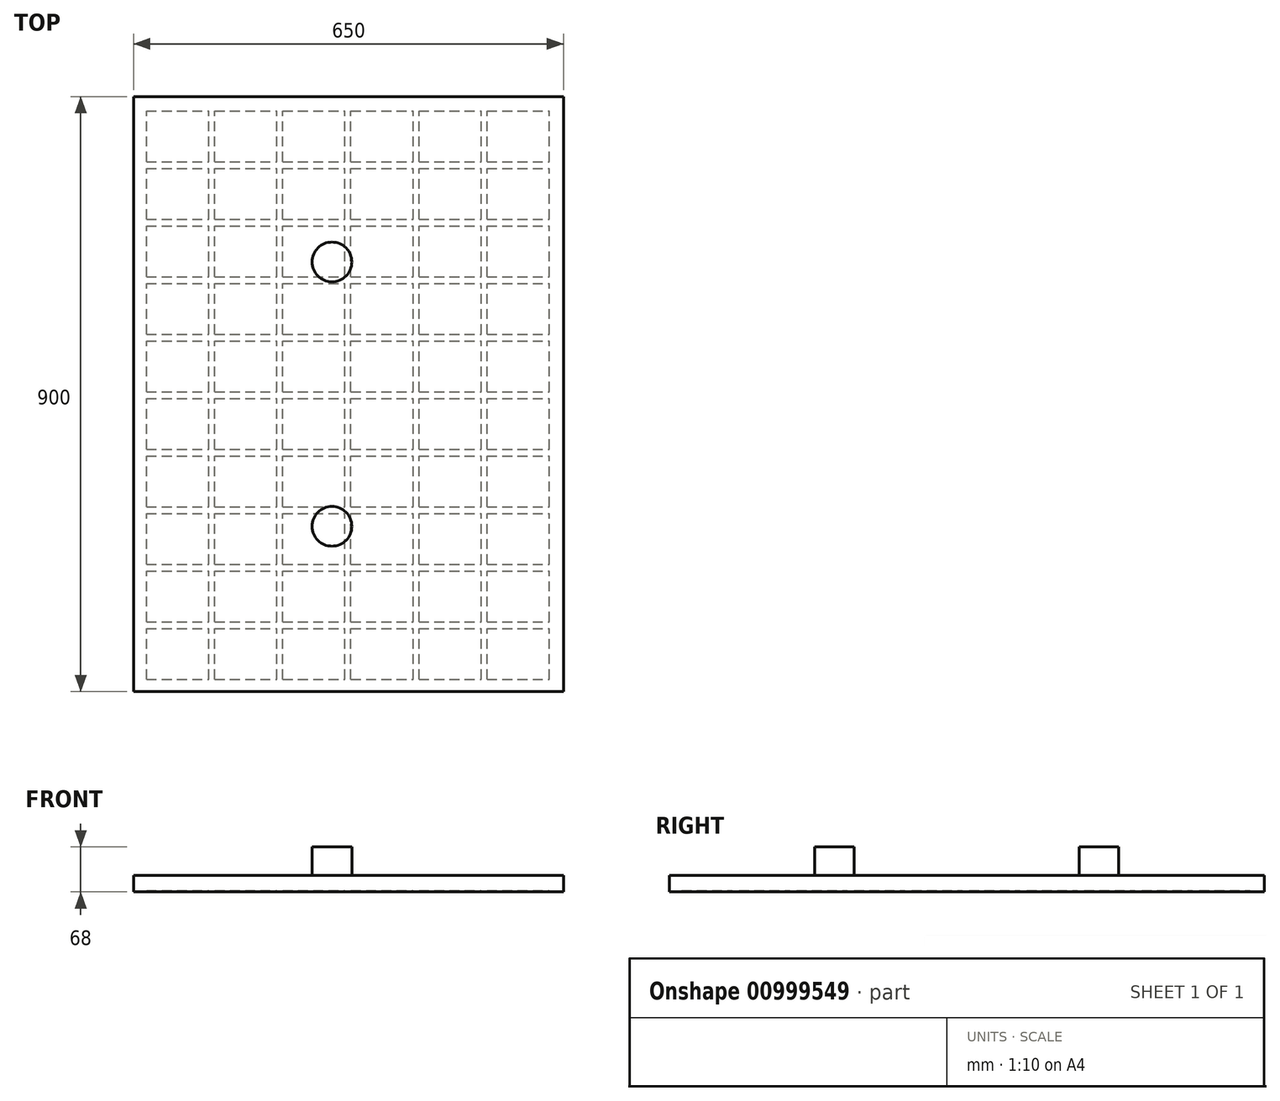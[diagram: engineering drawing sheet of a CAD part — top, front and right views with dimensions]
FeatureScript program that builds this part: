
annotation { "Feature Type Name" : "Feature", "Feature Type Description" : "" }
export const myFeature = defineFeature(function(context is Context, id is Id, definition is map)
    precondition{}
    {
        {
            var Q0;
            Q0=qCreatedBy(makeId("Top.planeOp"),FACE);
            var sketch = newSketch(context, id + "F0", { "sketchPlane" : qUnion([Q0])});
            skLineSegment(sketch, "E0.bottom", {"start": v(-300, 450) * mm, "end": v(350, 450) * mm});
            skLineSegment(sketch, "E0.top", {"start": v(-300, -450) * mm, "end": v(350, -450) * mm});
            skLineSegment(sketch, "E0.left", {"start": v(-300, 450) * mm, "end": v(-300, -450) * mm});
            skLineSegment(sketch, "E0.right", {"start": v(350, 450) * mm, "end": v(350, -450) * mm});
            skSolve(sketch);
        }
        {
            var Q0;
            Q0 = qSketchRegion(id + "F0", true);
            extrude(context, id + "F1", {"entities" : qUnion([Q0]), "depth" : 25 * mm, "offsetDistance" : 25 * mm});
        }
        {
            var Q0;
            Q0=makeQuery(id+"F1.opExtrude","CAP_FACE",FACE,{"disambiguationData":[OSD([sQuery(id+"F0.wireOp",EDGE,"E0.bottom"),sQuery(id+"F0.wireOp",EDGE,"E0.top"),sQuery(id+"F0.wireOp",EDGE,"E0.left"),sQuery(id+"F0.wireOp",EDGE,"E0.right")])],"isStart":false});
            var sketch = newSketch(context, id + "F2", { "sketchPlane" : qUnion([Q0])});
            skCircle(sketch, "E1", {"center": v(0, 200) * mm, "radius": 30 * mm});
            skCircle(sketch, "E2", {"center": v(0, -200) * mm, "radius": 30 * mm});
            skSolve(sketch);
        }
        {
            var Q0;
            Q0 = qSketchRegion(id + "F2", true);
            extrude(context, id + "F3", {"entities" : qUnion([Q0]), "operationType" : NewBodyOperationType.ADD, "depth" : 43 * mm, "offsetDistance" : 25 * mm});
        }
        {
            var Q0;
            Q0=makeQuery(id+"F1.opExtrude","CAP_FACE",FACE,{"disambiguationData":[OSD([sQuery(id+"F0.wireOp",EDGE,"E0.bottom"),sQuery(id+"F0.wireOp",EDGE,"E0.top"),sQuery(id+"F0.wireOp",EDGE,"E0.left"),sQuery(id+"F0.wireOp",EDGE,"E0.right")])],"isStart":true});
            var sketch = newSketch(context, id + "F4", { "sketchPlane" : qUnion([Q0])});
            skLineSegment(sketch, "E3.bottom", {"start": v(-280.37, 431.23) * mm, "end": v(-186.33, 431.23) * mm});
            skLineSegment(sketch, "E3.top", {"start": v(-280.37, 354.51) * mm, "end": v(-186.33, 354.51) * mm});
            skLineSegment(sketch, "E3.left", {"start": v(-280.37, 431.23) * mm, "end": v(-280.37, 354.51) * mm});
            skLineSegment(sketch, "E3.right", {"start": v(-186.33, 431.23) * mm, "end": v(-186.33, 354.51) * mm});
            skLineSegment(sketch, "E4.0.1.0", {"start": v(-280.37, 344.23) * mm, "end": v(-186.33, 344.23) * mm});
            skLineSegment(sketch, "E4.0.1.1", {"start": v(-186.33, 344.23) * mm, "end": v(-186.33, 267.51) * mm});
            skLineSegment(sketch, "E4.0.1.2", {"start": v(-280.37, 267.51) * mm, "end": v(-186.33, 267.51) * mm});
            skLineSegment(sketch, "E4.0.1.3", {"start": v(-280.37, 344.23) * mm, "end": v(-280.37, 267.51) * mm});
            skLineSegment(sketch, "E4.0.2.0", {"start": v(-280.37, 257.23) * mm, "end": v(-186.33, 257.23) * mm});
            skLineSegment(sketch, "E4.0.2.1", {"start": v(-186.33, 257.23) * mm, "end": v(-186.33, 180.51) * mm});
            skLineSegment(sketch, "E4.0.2.2", {"start": v(-280.37, 180.51) * mm, "end": v(-186.33, 180.51) * mm});
            skLineSegment(sketch, "E4.0.2.3", {"start": v(-280.37, 257.23) * mm, "end": v(-280.37, 180.51) * mm});
            skLineSegment(sketch, "E4.0.3.0", {"start": v(-280.37, 170.23) * mm, "end": v(-186.33, 170.23) * mm});
            skLineSegment(sketch, "E4.0.3.1", {"start": v(-186.33, 170.23) * mm, "end": v(-186.33, 93.51) * mm});
            skLineSegment(sketch, "E4.0.3.2", {"start": v(-280.37, 93.51) * mm, "end": v(-186.33, 93.51) * mm});
            skLineSegment(sketch, "E4.0.3.3", {"start": v(-280.37, 170.23) * mm, "end": v(-280.37, 93.51) * mm});
            skLineSegment(sketch, "E4.0.4.0", {"start": v(-280.37, 83.23) * mm, "end": v(-186.33, 83.23) * mm});
            skLineSegment(sketch, "E4.0.4.1", {"start": v(-186.33, 83.23) * mm, "end": v(-186.33, 6.51) * mm});
            skLineSegment(sketch, "E4.0.4.2", {"start": v(-280.37, 6.51) * mm, "end": v(-186.33, 6.51) * mm});
            skLineSegment(sketch, "E4.0.4.3", {"start": v(-280.37, 83.23) * mm, "end": v(-280.37, 6.51) * mm});
            skLineSegment(sketch, "E4.0.5.0", {"start": v(-280.37, -3.77) * mm, "end": v(-186.33, -3.77) * mm});
            skLineSegment(sketch, "E4.0.5.1", {"start": v(-186.33, -3.77) * mm, "end": v(-186.33, -80.49) * mm});
            skLineSegment(sketch, "E4.0.5.2", {"start": v(-280.37, -80.49) * mm, "end": v(-186.33, -80.49) * mm});
            skLineSegment(sketch, "E4.0.5.3", {"start": v(-280.37, -3.77) * mm, "end": v(-280.37, -80.49) * mm});
            skLineSegment(sketch, "E4.0.6.0", {"start": v(-280.37, -90.77) * mm, "end": v(-186.33, -90.77) * mm});
            skLineSegment(sketch, "E4.0.6.1", {"start": v(-186.33, -90.77) * mm, "end": v(-186.33, -167.49) * mm});
            skLineSegment(sketch, "E4.0.6.2", {"start": v(-280.37, -167.49) * mm, "end": v(-186.33, -167.49) * mm});
            skLineSegment(sketch, "E4.0.6.3", {"start": v(-280.37, -90.77) * mm, "end": v(-280.37, -167.49) * mm});
            skLineSegment(sketch, "E4.0.7.0", {"start": v(-280.37, -177.77) * mm, "end": v(-186.33, -177.77) * mm});
            skLineSegment(sketch, "E4.0.7.1", {"start": v(-186.33, -177.77) * mm, "end": v(-186.33, -254.49) * mm});
            skLineSegment(sketch, "E4.0.7.2", {"start": v(-280.37, -254.49) * mm, "end": v(-186.33, -254.49) * mm});
            skLineSegment(sketch, "E4.0.7.3", {"start": v(-280.37, -177.77) * mm, "end": v(-280.37, -254.49) * mm});
            skLineSegment(sketch, "E4.0.8.0", {"start": v(-280.37, -264.77) * mm, "end": v(-186.33, -264.77) * mm});
            skLineSegment(sketch, "E4.0.8.1", {"start": v(-186.33, -264.77) * mm, "end": v(-186.33, -341.49) * mm});
            skLineSegment(sketch, "E4.0.8.2", {"start": v(-280.37, -341.49) * mm, "end": v(-186.33, -341.49) * mm});
            skLineSegment(sketch, "E4.0.8.3", {"start": v(-280.37, -264.77) * mm, "end": v(-280.37, -341.49) * mm});
            skLineSegment(sketch, "E4.0.9.0", {"start": v(-280.37, -351.77) * mm, "end": v(-186.33, -351.77) * mm});
            skLineSegment(sketch, "E4.0.9.1", {"start": v(-186.33, -351.77) * mm, "end": v(-186.33, -428.49) * mm});
            skLineSegment(sketch, "E4.0.9.2", {"start": v(-280.37, -428.49) * mm, "end": v(-186.33, -428.49) * mm});
            skLineSegment(sketch, "E4.0.9.3", {"start": v(-280.37, -351.77) * mm, "end": v(-280.37, -428.49) * mm});
            skLineSegment(sketch, "E4.1.0.0", {"start": v(-177.37, 431.23) * mm, "end": v(-83.33, 431.23) * mm});
            skLineSegment(sketch, "E4.1.0.1", {"start": v(-83.33, 431.23) * mm, "end": v(-83.33, 354.51) * mm});
            skLineSegment(sketch, "E4.1.0.2", {"start": v(-177.37, 354.51) * mm, "end": v(-83.33, 354.51) * mm});
            skLineSegment(sketch, "E4.1.0.3", {"start": v(-177.37, 431.23) * mm, "end": v(-177.37, 354.51) * mm});
            skLineSegment(sketch, "E4.1.1.0", {"start": v(-177.37, 344.23) * mm, "end": v(-83.33, 344.23) * mm});
            skLineSegment(sketch, "E4.1.1.1", {"start": v(-83.33, 344.23) * mm, "end": v(-83.33, 267.51) * mm});
            skLineSegment(sketch, "E4.1.1.2", {"start": v(-177.37, 267.51) * mm, "end": v(-83.33, 267.51) * mm});
            skLineSegment(sketch, "E4.1.1.3", {"start": v(-177.37, 344.23) * mm, "end": v(-177.37, 267.51) * mm});
            skLineSegment(sketch, "E4.1.2.0", {"start": v(-177.37, 257.23) * mm, "end": v(-83.33, 257.23) * mm});
            skLineSegment(sketch, "E4.1.2.1", {"start": v(-83.33, 257.23) * mm, "end": v(-83.33, 180.51) * mm});
            skLineSegment(sketch, "E4.1.2.2", {"start": v(-177.37, 180.51) * mm, "end": v(-83.33, 180.51) * mm});
            skLineSegment(sketch, "E4.1.2.3", {"start": v(-177.37, 257.23) * mm, "end": v(-177.37, 180.51) * mm});
            skLineSegment(sketch, "E4.1.3.0", {"start": v(-177.37, 170.23) * mm, "end": v(-83.33, 170.23) * mm});
            skLineSegment(sketch, "E4.1.3.1", {"start": v(-83.33, 170.23) * mm, "end": v(-83.33, 93.51) * mm});
            skLineSegment(sketch, "E4.1.3.2", {"start": v(-177.37, 93.51) * mm, "end": v(-83.33, 93.51) * mm});
            skLineSegment(sketch, "E4.1.3.3", {"start": v(-177.37, 170.23) * mm, "end": v(-177.37, 93.51) * mm});
            skLineSegment(sketch, "E4.1.4.0", {"start": v(-177.37, 83.23) * mm, "end": v(-83.33, 83.23) * mm});
            skLineSegment(sketch, "E4.1.4.1", {"start": v(-83.33, 83.23) * mm, "end": v(-83.33, 6.51) * mm});
            skLineSegment(sketch, "E4.1.4.2", {"start": v(-177.37, 6.51) * mm, "end": v(-83.33, 6.51) * mm});
            skLineSegment(sketch, "E4.1.4.3", {"start": v(-177.37, 83.23) * mm, "end": v(-177.37, 6.51) * mm});
            skLineSegment(sketch, "E4.1.5.0", {"start": v(-177.37, -3.77) * mm, "end": v(-83.33, -3.77) * mm});
            skLineSegment(sketch, "E4.1.5.1", {"start": v(-83.33, -3.77) * mm, "end": v(-83.33, -80.49) * mm});
            skLineSegment(sketch, "E4.1.5.2", {"start": v(-177.37, -80.49) * mm, "end": v(-83.33, -80.49) * mm});
            skLineSegment(sketch, "E4.1.5.3", {"start": v(-177.37, -3.77) * mm, "end": v(-177.37, -80.49) * mm});
            skLineSegment(sketch, "E4.1.6.0", {"start": v(-177.37, -90.77) * mm, "end": v(-83.33, -90.77) * mm});
            skLineSegment(sketch, "E4.1.6.1", {"start": v(-83.33, -90.77) * mm, "end": v(-83.33, -167.49) * mm});
            skLineSegment(sketch, "E4.1.6.2", {"start": v(-177.37, -167.49) * mm, "end": v(-83.33, -167.49) * mm});
            skLineSegment(sketch, "E4.1.6.3", {"start": v(-177.37, -90.77) * mm, "end": v(-177.37, -167.49) * mm});
            skLineSegment(sketch, "E4.1.7.0", {"start": v(-177.37, -177.77) * mm, "end": v(-83.33, -177.77) * mm});
            skLineSegment(sketch, "E4.1.7.1", {"start": v(-83.33, -177.77) * mm, "end": v(-83.33, -254.49) * mm});
            skLineSegment(sketch, "E4.1.7.2", {"start": v(-177.37, -254.49) * mm, "end": v(-83.33, -254.49) * mm});
            skLineSegment(sketch, "E4.1.7.3", {"start": v(-177.37, -177.77) * mm, "end": v(-177.37, -254.49) * mm});
            skLineSegment(sketch, "E4.1.8.0", {"start": v(-177.37, -264.77) * mm, "end": v(-83.33, -264.77) * mm});
            skLineSegment(sketch, "E4.1.8.1", {"start": v(-83.33, -264.77) * mm, "end": v(-83.33, -341.49) * mm});
            skLineSegment(sketch, "E4.1.8.2", {"start": v(-177.37, -341.49) * mm, "end": v(-83.33, -341.49) * mm});
            skLineSegment(sketch, "E4.1.8.3", {"start": v(-177.37, -264.77) * mm, "end": v(-177.37, -341.49) * mm});
            skLineSegment(sketch, "E4.1.9.0", {"start": v(-177.37, -351.77) * mm, "end": v(-83.33, -351.77) * mm});
            skLineSegment(sketch, "E4.1.9.1", {"start": v(-83.33, -351.77) * mm, "end": v(-83.33, -428.49) * mm});
            skLineSegment(sketch, "E4.1.9.2", {"start": v(-177.37, -428.49) * mm, "end": v(-83.33, -428.49) * mm});
            skLineSegment(sketch, "E4.1.9.3", {"start": v(-177.37, -351.77) * mm, "end": v(-177.37, -428.49) * mm});
            skLineSegment(sketch, "E4.2.0.0", {"start": v(-74.37, 431.23) * mm, "end": v(19.67, 431.23) * mm});
            skLineSegment(sketch, "E4.2.0.1", {"start": v(19.67, 431.23) * mm, "end": v(19.67, 354.51) * mm});
            skLineSegment(sketch, "E4.2.0.2", {"start": v(-74.37, 354.51) * mm, "end": v(19.67, 354.51) * mm});
            skLineSegment(sketch, "E4.2.0.3", {"start": v(-74.37, 431.23) * mm, "end": v(-74.37, 354.51) * mm});
            skLineSegment(sketch, "E4.2.1.0", {"start": v(-74.37, 344.23) * mm, "end": v(19.67, 344.23) * mm});
            skLineSegment(sketch, "E4.2.1.1", {"start": v(19.67, 344.23) * mm, "end": v(19.67, 267.51) * mm});
            skLineSegment(sketch, "E4.2.1.2", {"start": v(-74.37, 267.51) * mm, "end": v(19.67, 267.51) * mm});
            skLineSegment(sketch, "E4.2.1.3", {"start": v(-74.37, 344.23) * mm, "end": v(-74.37, 267.51) * mm});
            skLineSegment(sketch, "E4.2.2.0", {"start": v(-74.37, 257.23) * mm, "end": v(19.67, 257.23) * mm});
            skLineSegment(sketch, "E4.2.2.1", {"start": v(19.67, 257.23) * mm, "end": v(19.67, 180.51) * mm});
            skLineSegment(sketch, "E4.2.2.2", {"start": v(-74.37, 180.51) * mm, "end": v(19.67, 180.51) * mm});
            skLineSegment(sketch, "E4.2.2.3", {"start": v(-74.37, 257.23) * mm, "end": v(-74.37, 180.51) * mm});
            skLineSegment(sketch, "E4.2.3.0", {"start": v(-74.37, 170.23) * mm, "end": v(19.67, 170.23) * mm});
            skLineSegment(sketch, "E4.2.3.1", {"start": v(19.67, 170.23) * mm, "end": v(19.67, 93.51) * mm});
            skLineSegment(sketch, "E4.2.3.2", {"start": v(-74.37, 93.51) * mm, "end": v(19.67, 93.51) * mm});
            skLineSegment(sketch, "E4.2.3.3", {"start": v(-74.37, 170.23) * mm, "end": v(-74.37, 93.51) * mm});
            skLineSegment(sketch, "E4.2.4.0", {"start": v(-74.37, 83.23) * mm, "end": v(19.67, 83.23) * mm});
            skLineSegment(sketch, "E4.2.4.1", {"start": v(19.67, 83.23) * mm, "end": v(19.67, 6.51) * mm});
            skLineSegment(sketch, "E4.2.4.2", {"start": v(-74.37, 6.51) * mm, "end": v(19.67, 6.51) * mm});
            skLineSegment(sketch, "E4.2.4.3", {"start": v(-74.37, 83.23) * mm, "end": v(-74.37, 6.51) * mm});
            skLineSegment(sketch, "E4.2.5.0", {"start": v(-74.37, -3.77) * mm, "end": v(19.67, -3.77) * mm});
            skLineSegment(sketch, "E4.2.5.1", {"start": v(19.67, -3.77) * mm, "end": v(19.67, -80.49) * mm});
            skLineSegment(sketch, "E4.2.5.2", {"start": v(-74.37, -80.49) * mm, "end": v(19.67, -80.49) * mm});
            skLineSegment(sketch, "E4.2.5.3", {"start": v(-74.37, -3.77) * mm, "end": v(-74.37, -80.49) * mm});
            skLineSegment(sketch, "E4.2.6.0", {"start": v(-74.37, -90.77) * mm, "end": v(19.67, -90.77) * mm});
            skLineSegment(sketch, "E4.2.6.1", {"start": v(19.67, -90.77) * mm, "end": v(19.67, -167.49) * mm});
            skLineSegment(sketch, "E4.2.6.2", {"start": v(-74.37, -167.49) * mm, "end": v(19.67, -167.49) * mm});
            skLineSegment(sketch, "E4.2.6.3", {"start": v(-74.37, -90.77) * mm, "end": v(-74.37, -167.49) * mm});
            skLineSegment(sketch, "E4.2.7.0", {"start": v(-74.37, -177.77) * mm, "end": v(19.67, -177.77) * mm});
            skLineSegment(sketch, "E4.2.7.1", {"start": v(19.67, -177.77) * mm, "end": v(19.67, -254.49) * mm});
            skLineSegment(sketch, "E4.2.7.2", {"start": v(-74.37, -254.49) * mm, "end": v(19.67, -254.49) * mm});
            skLineSegment(sketch, "E4.2.7.3", {"start": v(-74.37, -177.77) * mm, "end": v(-74.37, -254.49) * mm});
            skLineSegment(sketch, "E4.2.8.0", {"start": v(-74.37, -264.77) * mm, "end": v(19.67, -264.77) * mm});
            skLineSegment(sketch, "E4.2.8.1", {"start": v(19.67, -264.77) * mm, "end": v(19.67, -341.49) * mm});
            skLineSegment(sketch, "E4.2.8.2", {"start": v(-74.37, -341.49) * mm, "end": v(19.67, -341.49) * mm});
            skLineSegment(sketch, "E4.2.8.3", {"start": v(-74.37, -264.77) * mm, "end": v(-74.37, -341.49) * mm});
            skLineSegment(sketch, "E4.2.9.0", {"start": v(-74.37, -351.77) * mm, "end": v(19.67, -351.77) * mm});
            skLineSegment(sketch, "E4.2.9.1", {"start": v(19.67, -351.77) * mm, "end": v(19.67, -428.49) * mm});
            skLineSegment(sketch, "E4.2.9.2", {"start": v(-74.37, -428.49) * mm, "end": v(19.67, -428.49) * mm});
            skLineSegment(sketch, "E4.2.9.3", {"start": v(-74.37, -351.77) * mm, "end": v(-74.37, -428.49) * mm});
            skLineSegment(sketch, "E4.3.0.0", {"start": v(28.63, 431.23) * mm, "end": v(122.67, 431.23) * mm});
            skLineSegment(sketch, "E4.3.0.1", {"start": v(122.67, 431.23) * mm, "end": v(122.67, 354.51) * mm});
            skLineSegment(sketch, "E4.3.0.2", {"start": v(28.63, 354.51) * mm, "end": v(122.67, 354.51) * mm});
            skLineSegment(sketch, "E4.3.0.3", {"start": v(28.63, 431.23) * mm, "end": v(28.63, 354.51) * mm});
            skLineSegment(sketch, "E4.3.1.0", {"start": v(28.63, 344.23) * mm, "end": v(122.67, 344.23) * mm});
            skLineSegment(sketch, "E4.3.1.1", {"start": v(122.67, 344.23) * mm, "end": v(122.67, 267.51) * mm});
            skLineSegment(sketch, "E4.3.1.2", {"start": v(28.63, 267.51) * mm, "end": v(122.67, 267.51) * mm});
            skLineSegment(sketch, "E4.3.1.3", {"start": v(28.63, 344.23) * mm, "end": v(28.63, 267.51) * mm});
            skLineSegment(sketch, "E4.3.2.0", {"start": v(28.63, 257.23) * mm, "end": v(122.67, 257.23) * mm});
            skLineSegment(sketch, "E4.3.2.1", {"start": v(122.67, 257.23) * mm, "end": v(122.67, 180.51) * mm});
            skLineSegment(sketch, "E4.3.2.2", {"start": v(28.63, 180.51) * mm, "end": v(122.67, 180.51) * mm});
            skLineSegment(sketch, "E4.3.2.3", {"start": v(28.63, 257.23) * mm, "end": v(28.63, 180.51) * mm});
            skLineSegment(sketch, "E4.3.3.0", {"start": v(28.63, 170.23) * mm, "end": v(122.67, 170.23) * mm});
            skLineSegment(sketch, "E4.3.3.1", {"start": v(122.67, 170.23) * mm, "end": v(122.67, 93.51) * mm});
            skLineSegment(sketch, "E4.3.3.2", {"start": v(28.63, 93.51) * mm, "end": v(122.67, 93.51) * mm});
            skLineSegment(sketch, "E4.3.3.3", {"start": v(28.63, 170.23) * mm, "end": v(28.63, 93.51) * mm});
            skLineSegment(sketch, "E4.3.4.0", {"start": v(28.63, 83.23) * mm, "end": v(122.67, 83.23) * mm});
            skLineSegment(sketch, "E4.3.4.1", {"start": v(122.67, 83.23) * mm, "end": v(122.67, 6.51) * mm});
            skLineSegment(sketch, "E4.3.4.2", {"start": v(28.63, 6.51) * mm, "end": v(122.67, 6.51) * mm});
            skLineSegment(sketch, "E4.3.4.3", {"start": v(28.63, 83.23) * mm, "end": v(28.63, 6.51) * mm});
            skLineSegment(sketch, "E4.3.5.0", {"start": v(28.63, -3.77) * mm, "end": v(122.67, -3.77) * mm});
            skLineSegment(sketch, "E4.3.5.1", {"start": v(122.67, -3.77) * mm, "end": v(122.67, -80.49) * mm});
            skLineSegment(sketch, "E4.3.5.2", {"start": v(28.63, -80.49) * mm, "end": v(122.67, -80.49) * mm});
            skLineSegment(sketch, "E4.3.5.3", {"start": v(28.63, -3.77) * mm, "end": v(28.63, -80.49) * mm});
            skLineSegment(sketch, "E4.3.6.0", {"start": v(28.63, -90.77) * mm, "end": v(122.67, -90.77) * mm});
            skLineSegment(sketch, "E4.3.6.1", {"start": v(122.67, -90.77) * mm, "end": v(122.67, -167.49) * mm});
            skLineSegment(sketch, "E4.3.6.2", {"start": v(28.63, -167.49) * mm, "end": v(122.67, -167.49) * mm});
            skLineSegment(sketch, "E4.3.6.3", {"start": v(28.63, -90.77) * mm, "end": v(28.63, -167.49) * mm});
            skLineSegment(sketch, "E4.3.7.0", {"start": v(28.63, -177.77) * mm, "end": v(122.67, -177.77) * mm});
            skLineSegment(sketch, "E4.3.7.1", {"start": v(122.67, -177.77) * mm, "end": v(122.67, -254.49) * mm});
            skLineSegment(sketch, "E4.3.7.2", {"start": v(28.63, -254.49) * mm, "end": v(122.67, -254.49) * mm});
            skLineSegment(sketch, "E4.3.7.3", {"start": v(28.63, -177.77) * mm, "end": v(28.63, -254.49) * mm});
            skLineSegment(sketch, "E4.3.8.0", {"start": v(28.63, -264.77) * mm, "end": v(122.67, -264.77) * mm});
            skLineSegment(sketch, "E4.3.8.1", {"start": v(122.67, -264.77) * mm, "end": v(122.67, -341.49) * mm});
            skLineSegment(sketch, "E4.3.8.2", {"start": v(28.63, -341.49) * mm, "end": v(122.67, -341.49) * mm});
            skLineSegment(sketch, "E4.3.8.3", {"start": v(28.63, -264.77) * mm, "end": v(28.63, -341.49) * mm});
            skLineSegment(sketch, "E4.3.9.0", {"start": v(28.63, -351.77) * mm, "end": v(122.67, -351.77) * mm});
            skLineSegment(sketch, "E4.3.9.1", {"start": v(122.67, -351.77) * mm, "end": v(122.67, -428.49) * mm});
            skLineSegment(sketch, "E4.3.9.2", {"start": v(28.63, -428.49) * mm, "end": v(122.67, -428.49) * mm});
            skLineSegment(sketch, "E4.3.9.3", {"start": v(28.63, -351.77) * mm, "end": v(28.63, -428.49) * mm});
            skLineSegment(sketch, "E4.4.0.0", {"start": v(131.63, 431.23) * mm, "end": v(225.67, 431.23) * mm});
            skLineSegment(sketch, "E4.4.0.1", {"start": v(225.67, 431.23) * mm, "end": v(225.67, 354.51) * mm});
            skLineSegment(sketch, "E4.4.0.2", {"start": v(131.63, 354.51) * mm, "end": v(225.67, 354.51) * mm});
            skLineSegment(sketch, "E4.4.0.3", {"start": v(131.63, 431.23) * mm, "end": v(131.63, 354.51) * mm});
            skLineSegment(sketch, "E4.4.1.0", {"start": v(131.63, 344.23) * mm, "end": v(225.67, 344.23) * mm});
            skLineSegment(sketch, "E4.4.1.1", {"start": v(225.67, 344.23) * mm, "end": v(225.67, 267.51) * mm});
            skLineSegment(sketch, "E4.4.1.2", {"start": v(131.63, 267.51) * mm, "end": v(225.67, 267.51) * mm});
            skLineSegment(sketch, "E4.4.1.3", {"start": v(131.63, 344.23) * mm, "end": v(131.63, 267.51) * mm});
            skLineSegment(sketch, "E4.4.2.0", {"start": v(131.63, 257.23) * mm, "end": v(225.67, 257.23) * mm});
            skLineSegment(sketch, "E4.4.2.1", {"start": v(225.67, 257.23) * mm, "end": v(225.67, 180.51) * mm});
            skLineSegment(sketch, "E4.4.2.2", {"start": v(131.63, 180.51) * mm, "end": v(225.67, 180.51) * mm});
            skLineSegment(sketch, "E4.4.2.3", {"start": v(131.63, 257.23) * mm, "end": v(131.63, 180.51) * mm});
            skLineSegment(sketch, "E4.4.3.0", {"start": v(131.63, 170.23) * mm, "end": v(225.67, 170.23) * mm});
            skLineSegment(sketch, "E4.4.3.1", {"start": v(225.67, 170.23) * mm, "end": v(225.67, 93.51) * mm});
            skLineSegment(sketch, "E4.4.3.2", {"start": v(131.63, 93.51) * mm, "end": v(225.67, 93.51) * mm});
            skLineSegment(sketch, "E4.4.3.3", {"start": v(131.63, 170.23) * mm, "end": v(131.63, 93.51) * mm});
            skLineSegment(sketch, "E4.4.4.0", {"start": v(131.63, 83.23) * mm, "end": v(225.67, 83.23) * mm});
            skLineSegment(sketch, "E4.4.4.1", {"start": v(225.67, 83.23) * mm, "end": v(225.67, 6.51) * mm});
            skLineSegment(sketch, "E4.4.4.2", {"start": v(131.63, 6.51) * mm, "end": v(225.67, 6.51) * mm});
            skLineSegment(sketch, "E4.4.4.3", {"start": v(131.63, 83.23) * mm, "end": v(131.63, 6.51) * mm});
            skLineSegment(sketch, "E4.4.5.0", {"start": v(131.63, -3.77) * mm, "end": v(225.67, -3.77) * mm});
            skLineSegment(sketch, "E4.4.5.1", {"start": v(225.67, -3.77) * mm, "end": v(225.67, -80.49) * mm});
            skLineSegment(sketch, "E4.4.5.2", {"start": v(131.63, -80.49) * mm, "end": v(225.67, -80.49) * mm});
            skLineSegment(sketch, "E4.4.5.3", {"start": v(131.63, -3.77) * mm, "end": v(131.63, -80.49) * mm});
            skLineSegment(sketch, "E4.4.6.0", {"start": v(131.63, -90.77) * mm, "end": v(225.67, -90.77) * mm});
            skLineSegment(sketch, "E4.4.6.1", {"start": v(225.67, -90.77) * mm, "end": v(225.67, -167.49) * mm});
            skLineSegment(sketch, "E4.4.6.2", {"start": v(131.63, -167.49) * mm, "end": v(225.67, -167.49) * mm});
            skLineSegment(sketch, "E4.4.6.3", {"start": v(131.63, -90.77) * mm, "end": v(131.63, -167.49) * mm});
            skLineSegment(sketch, "E4.4.7.0", {"start": v(131.63, -177.77) * mm, "end": v(225.67, -177.77) * mm});
            skLineSegment(sketch, "E4.4.7.1", {"start": v(225.67, -177.77) * mm, "end": v(225.67, -254.49) * mm});
            skLineSegment(sketch, "E4.4.7.2", {"start": v(131.63, -254.49) * mm, "end": v(225.67, -254.49) * mm});
            skLineSegment(sketch, "E4.4.7.3", {"start": v(131.63, -177.77) * mm, "end": v(131.63, -254.49) * mm});
            skLineSegment(sketch, "E4.4.8.0", {"start": v(131.63, -264.77) * mm, "end": v(225.67, -264.77) * mm});
            skLineSegment(sketch, "E4.4.8.1", {"start": v(225.67, -264.77) * mm, "end": v(225.67, -341.49) * mm});
            skLineSegment(sketch, "E4.4.8.2", {"start": v(131.63, -341.49) * mm, "end": v(225.67, -341.49) * mm});
            skLineSegment(sketch, "E4.4.8.3", {"start": v(131.63, -264.77) * mm, "end": v(131.63, -341.49) * mm});
            skLineSegment(sketch, "E4.4.9.0", {"start": v(131.63, -351.77) * mm, "end": v(225.67, -351.77) * mm});
            skLineSegment(sketch, "E4.4.9.1", {"start": v(225.67, -351.77) * mm, "end": v(225.67, -428.49) * mm});
            skLineSegment(sketch, "E4.4.9.2", {"start": v(131.63, -428.49) * mm, "end": v(225.67, -428.49) * mm});
            skLineSegment(sketch, "E4.4.9.3", {"start": v(131.63, -351.77) * mm, "end": v(131.63, -428.49) * mm});
            skLineSegment(sketch, "E4.5.0.0", {"start": v(234.63, 431.23) * mm, "end": v(328.67, 431.23) * mm});
            skLineSegment(sketch, "E4.5.0.1", {"start": v(328.67, 431.23) * mm, "end": v(328.67, 354.51) * mm});
            skLineSegment(sketch, "E4.5.0.2", {"start": v(234.63, 354.51) * mm, "end": v(328.67, 354.51) * mm});
            skLineSegment(sketch, "E4.5.0.3", {"start": v(234.63, 431.23) * mm, "end": v(234.63, 354.51) * mm});
            skLineSegment(sketch, "E4.5.1.0", {"start": v(234.63, 344.23) * mm, "end": v(328.67, 344.23) * mm});
            skLineSegment(sketch, "E4.5.1.1", {"start": v(328.67, 344.23) * mm, "end": v(328.67, 267.51) * mm});
            skLineSegment(sketch, "E4.5.1.2", {"start": v(234.63, 267.51) * mm, "end": v(328.67, 267.51) * mm});
            skLineSegment(sketch, "E4.5.1.3", {"start": v(234.63, 344.23) * mm, "end": v(234.63, 267.51) * mm});
            skLineSegment(sketch, "E4.5.2.0", {"start": v(234.63, 257.23) * mm, "end": v(328.67, 257.23) * mm});
            skLineSegment(sketch, "E4.5.2.1", {"start": v(328.67, 257.23) * mm, "end": v(328.67, 180.51) * mm});
            skLineSegment(sketch, "E4.5.2.2", {"start": v(234.63, 180.51) * mm, "end": v(328.67, 180.51) * mm});
            skLineSegment(sketch, "E4.5.2.3", {"start": v(234.63, 257.23) * mm, "end": v(234.63, 180.51) * mm});
            skLineSegment(sketch, "E4.5.3.0", {"start": v(234.63, 170.23) * mm, "end": v(328.67, 170.23) * mm});
            skLineSegment(sketch, "E4.5.3.1", {"start": v(328.67, 170.23) * mm, "end": v(328.67, 93.51) * mm});
            skLineSegment(sketch, "E4.5.3.2", {"start": v(234.63, 93.51) * mm, "end": v(328.67, 93.51) * mm});
            skLineSegment(sketch, "E4.5.3.3", {"start": v(234.63, 170.23) * mm, "end": v(234.63, 93.51) * mm});
            skLineSegment(sketch, "E4.5.4.0", {"start": v(234.63, 83.23) * mm, "end": v(328.67, 83.23) * mm});
            skLineSegment(sketch, "E4.5.4.1", {"start": v(328.67, 83.23) * mm, "end": v(328.67, 6.51) * mm});
            skLineSegment(sketch, "E4.5.4.2", {"start": v(234.63, 6.51) * mm, "end": v(328.67, 6.51) * mm});
            skLineSegment(sketch, "E4.5.4.3", {"start": v(234.63, 83.23) * mm, "end": v(234.63, 6.51) * mm});
            skLineSegment(sketch, "E4.5.5.0", {"start": v(234.63, -3.77) * mm, "end": v(328.67, -3.77) * mm});
            skLineSegment(sketch, "E4.5.5.1", {"start": v(328.67, -3.77) * mm, "end": v(328.67, -80.49) * mm});
            skLineSegment(sketch, "E4.5.5.2", {"start": v(234.63, -80.49) * mm, "end": v(328.67, -80.49) * mm});
            skLineSegment(sketch, "E4.5.5.3", {"start": v(234.63, -3.77) * mm, "end": v(234.63, -80.49) * mm});
            skLineSegment(sketch, "E4.5.6.0", {"start": v(234.63, -90.77) * mm, "end": v(328.67, -90.77) * mm});
            skLineSegment(sketch, "E4.5.6.1", {"start": v(328.67, -90.77) * mm, "end": v(328.67, -167.49) * mm});
            skLineSegment(sketch, "E4.5.6.2", {"start": v(234.63, -167.49) * mm, "end": v(328.67, -167.49) * mm});
            skLineSegment(sketch, "E4.5.6.3", {"start": v(234.63, -90.77) * mm, "end": v(234.63, -167.49) * mm});
            skLineSegment(sketch, "E4.5.7.0", {"start": v(234.63, -177.77) * mm, "end": v(328.67, -177.77) * mm});
            skLineSegment(sketch, "E4.5.7.1", {"start": v(328.67, -177.77) * mm, "end": v(328.67, -254.49) * mm});
            skLineSegment(sketch, "E4.5.7.2", {"start": v(234.63, -254.49) * mm, "end": v(328.67, -254.49) * mm});
            skLineSegment(sketch, "E4.5.7.3", {"start": v(234.63, -177.77) * mm, "end": v(234.63, -254.49) * mm});
            skLineSegment(sketch, "E4.5.8.0", {"start": v(234.63, -264.77) * mm, "end": v(328.67, -264.77) * mm});
            skLineSegment(sketch, "E4.5.8.1", {"start": v(328.67, -264.77) * mm, "end": v(328.67, -341.49) * mm});
            skLineSegment(sketch, "E4.5.8.2", {"start": v(234.63, -341.49) * mm, "end": v(328.67, -341.49) * mm});
            skLineSegment(sketch, "E4.5.8.3", {"start": v(234.63, -264.77) * mm, "end": v(234.63, -341.49) * mm});
            skLineSegment(sketch, "E4.5.9.0", {"start": v(234.63, -351.77) * mm, "end": v(328.67, -351.77) * mm});
            skLineSegment(sketch, "E4.5.9.1", {"start": v(328.67, -351.77) * mm, "end": v(328.67, -428.49) * mm});
            skLineSegment(sketch, "E4.5.9.2", {"start": v(234.63, -428.49) * mm, "end": v(328.67, -428.49) * mm});
            skLineSegment(sketch, "E4.5.9.3", {"start": v(234.63, -351.77) * mm, "end": v(234.63, -428.49) * mm});
            skLineSegment(sketch, "E4.direction1", {"start": v(-280.37, 431.23) * mm, "end": v(-177.37, 431.23) * mm, "construction": true});
            skLineSegment(sketch, "E4.direction2", {"start": v(-280.37, 431.23) * mm, "end": v(-280.37, 344.23) * mm, "construction": true});
            skSolve(sketch);
        }
        {
            var Q0;
            Q0 = qSketchRegion(id + "F4", true);
            extrude(context, id + "F5", {"entities" : qUnion([Q0]), "operationType" : NewBodyOperationType.REMOVE, "oppositeDirection" : true, "depth" : 2 * mm, "offsetDistance" : 25 * mm});
        }
    });
